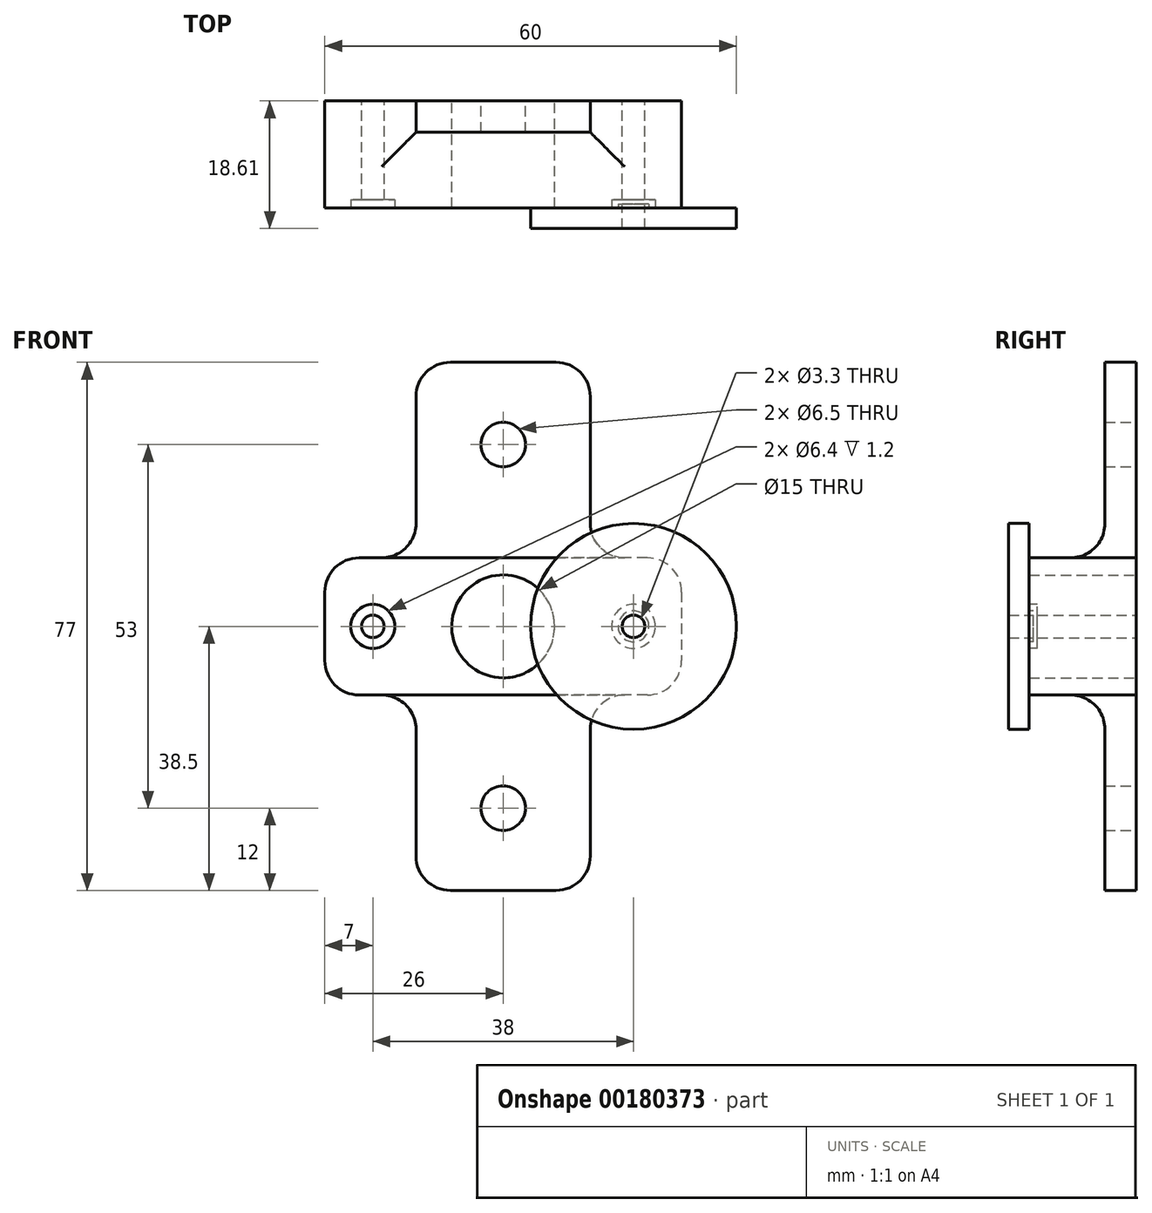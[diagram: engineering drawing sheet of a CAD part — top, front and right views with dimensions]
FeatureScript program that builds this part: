
annotation { "Feature Type Name" : "Feature", "Feature Type Description" : "" }
export const myFeature = defineFeature(function(context is Context, id is Id, definition is map)
    precondition{}
    {
        {
            var Q0;
            Q0=qCreatedBy(makeId("Front.planeOp"),FACE);
            var sketch = newSketch(context, id + "F0", { "sketchPlane" : qUnion([Q0])});
            skLineSegment(sketch, "E0.bottom", {"start": v(12.7, 38.5) * mm, "end": v(-12.7, 38.5) * mm});
            skLineSegment(sketch, "E0.top", {"start": v(12.7, -38.5) * mm, "end": v(-12.7, -38.5) * mm});
            skLineSegment(sketch, "E0.left", {"start": v(12.7, 38.5) * mm, "end": v(12.7, -38.5) * mm});
            skLineSegment(sketch, "E0.right", {"start": v(-12.7, 38.5) * mm, "end": v(-12.7, -38.5) * mm});
            skPoint(sketch, "E0.middle", {"position": v(0, 0) * mm});
            skLineSegment(sketch, "E1.bottom", {"start": v(26, 10) * mm, "end": v(-26, 10) * mm});
            skLineSegment(sketch, "E1.top", {"start": v(26, -10) * mm, "end": v(-26, -10) * mm});
            skLineSegment(sketch, "E1.left", {"start": v(26, 10) * mm, "end": v(26, -10) * mm});
            skLineSegment(sketch, "E1.right", {"start": v(-26, 10) * mm, "end": v(-26, -10) * mm});
            skCircle(sketch, "E2", {"center": v(0, 0) * mm, "radius": 7.5 * mm});
            skCircle(sketch, "E3", {"center": v(0, 26.5) * mm, "radius": 3.25 * mm});
            skLineSegment(sketch, "E4", {"start": v(0, 0) * mm, "end": v(26, 0) * mm, "construction": true});
            skCircle(sketch, "E5.MirrorC", {"center": v(0, -26.5) * mm, "radius": 3.25 * mm});
            skCircle(sketch, "E6", {"center": v(-19, 0) * mm, "radius": 1.65 * mm});
            skLineSegment(sketch, "E7", {"start": v(0, 0) * mm, "end": v(0, 26.5) * mm, "construction": true});
            skCircle(sketch, "E8.MirrorC", {"center": v(19, 0) * mm, "radius": 1.65 * mm});
            skSolve(sketch);
        }
        {
            var Q0;
            {var subQ5=sQuery(id+"F0.wireOp",EDGE,"E0.bottom");Q0=makeQuery(id+"F0.imprint","IMPRINT",FACE,{"disambiguationData":[TD([[makeQuery(id+"F0.imprint","IMPRINT",EDGE,{"derivedFrom":subQ5}),1.0]])]});}
            var Q1;
            {var subQ5=sQuery(id+"F0.wireOp",EDGE,"E0.top");Q1=makeQuery(id+"F0.imprint","IMPRINT",FACE,{"disambiguationData":[TD([[makeQuery(id+"F0.imprint","IMPRINT",EDGE,{"derivedFrom":subQ5}),-1.0]])]});}
            var Q2;
            Q2=makeQuery(id+"F0.imprint","IMPRINT",FACE,{"disambiguationData":[TD([[makeQuery(id+"F0.imprint","IMPRINT",EDGE,{"derivedFrom":sQuery(id+"F0.wireOp",EDGE,"E2")}),-1.0]])]});
            extrude(context, id + "F1", {"entities" : qUnion([Q0, Q1, Q2]), "depth" : 4.57 * mm, "offsetDistance" : 25 * mm});
        }
        {
            var Q0;
            {var subQ0=sQuery(id+"F0.wireOp",EDGE,"E1.left");Q0=makeQuery(id+"F0.imprint","IMPRINT",FACE,{"disambiguationData":[TD([[makeQuery(id+"F0.imprint","IMPRINT",EDGE,{"derivedFrom":subQ0}),-1.0]])]});}
            var Q1;
            {var subQ0=sQuery(id+"F0.wireOp",EDGE,"E1.right");Q1=makeQuery(id+"F0.imprint","IMPRINT",FACE,{"disambiguationData":[TD([[makeQuery(id+"F0.imprint","IMPRINT",EDGE,{"derivedFrom":subQ0}),1.0]])]});}
            var Q2;
            Q2=makeQuery(id+"F0.imprint","IMPRINT",FACE,{"disambiguationData":[TD([[makeQuery(id+"F0.imprint","IMPRINT",EDGE,{"derivedFrom":sQuery(id+"F0.wireOp",EDGE,"E2")}),-1.0]])]});
            extrude(context, id + "F2", {"entities" : qUnion([Q0, Q1, Q2]), "operationType" : NewBodyOperationType.ADD, "depth" : 15.6 * mm, "offsetDistance" : 25 * mm});
        }
        {
            var Q0;
            Q0=makeQuery(id+"F2.opExtrude","CAP_FACE",FACE,{"disambiguationData":[OSD([sQuery(id+"F0.wireOp",EDGE,"E1.bottom"),sQuery(id+"F0.wireOp",EDGE,"E1.top"),sQuery(id+"F0.wireOp",EDGE,"E1.left"),sQuery(id+"F0.wireOp",EDGE,"E1.right"),sQuery(id+"F0.wireOp",EDGE,"E2"),sQuery(id+"F0.wireOp",EDGE,"E6"),sQuery(id+"F0.wireOp",EDGE,"E8.MirrorC")])],"isStart":false});
            var sketch = newSketch(context, id + "F3", { "sketchPlane" : qUnion([Q0])});
            skCircle(sketch, "E9", {"center": v(19, 0) * mm, "radius": 3.2 * mm});
            skCircle(sketch, "E10", {"center": v(-19, 0) * mm, "radius": 3.2 * mm});
            skSolve(sketch);
        }
        {
            var Q0;
            Q0=makeQuery(id+"F3.imprint","IMPRINT",FACE,{"disambiguationData":[TD([[makeQuery(id+"F3.imprint","IMPRINT",EDGE,{"derivedFrom":sQuery(id+"F3.wireOp",EDGE,"E10")}),1.0]])]});
            var Q1;
            Q1=makeQuery(id+"F3.imprint","IMPRINT",FACE,{"disambiguationData":[TD([[makeQuery(id+"F3.imprint","IMPRINT",EDGE,{"derivedFrom":sQuery(id+"F3.wireOp",EDGE,"E9")}),1.0]])]});
            extrude(context, id + "F4", {"entities" : qUnion([Q0, Q1]), "operationType" : NewBodyOperationType.REMOVE, "oppositeDirection" : true, "depth" : 1.2 * mm, "offsetDistance" : 25 * mm});
        }
        {
            var Q0;
            Q0=makeQuery(id+"F2.boolean.opBoolean","INTERSECT",EDGE,{"derivedFrom":[makeQuery(id+"F1.opExtrude","CAP_FACE",FACE,{"disambiguationData":[OSD([sQuery(id+"F0.wireOp",EDGE,"E0.bottom"),sQuery(id+"F0.wireOp",EDGE,"E0.top"),sQuery(id+"F0.wireOp",EDGE,"E0.left"),sQuery(id+"F0.wireOp",EDGE,"E0.right"),sQuery(id+"F0.wireOp",EDGE,"E2"),sQuery(id+"F0.wireOp",EDGE,"E3"),sQuery(id+"F0.wireOp",EDGE,"E5.MirrorC")])],"isStart":false}),makeQuery(id+"F2.opExtrude","SWEPT_FACE",FACE,{"disambiguationData":[OSD([sQuery(id+"F0.wireOp",EDGE,"E1.bottom")])]})]});
            var Q1;
            Q1=makeQuery(id+"F2.boolean.opBoolean","INTERSECT",EDGE,{"derivedFrom":[makeQuery(id+"F1.opExtrude","CAP_FACE",FACE,{"disambiguationData":[OSD([sQuery(id+"F0.wireOp",EDGE,"E0.bottom"),sQuery(id+"F0.wireOp",EDGE,"E0.top"),sQuery(id+"F0.wireOp",EDGE,"E0.left"),sQuery(id+"F0.wireOp",EDGE,"E0.right"),sQuery(id+"F0.wireOp",EDGE,"E2"),sQuery(id+"F0.wireOp",EDGE,"E3"),sQuery(id+"F0.wireOp",EDGE,"E5.MirrorC")])],"isStart":false}),makeQuery(id+"F2.opExtrude","SWEPT_FACE",FACE,{"disambiguationData":[OSD([sQuery(id+"F0.wireOp",EDGE,"E1.top")])]})]});
            var Q2;
            Q2=makeQuery(id+"F2.opExtrude","SWEPT_EDGE",EDGE,{"disambiguationData":[OSD([sQuery(id+"F0.wireOp",EDGE,"E1.top"),sQuery(id+"F0.wireOp",EDGE,"E1.left")])]});
            var Q3;
            Q3=makeQuery(id+"F2.opExtrude","SWEPT_EDGE",EDGE,{"disambiguationData":[OSD([sQuery(id+"F0.wireOp",EDGE,"E1.top"),sQuery(id+"F0.wireOp",EDGE,"E1.right")])]});
            var Q4;
            Q4=makeQuery(id+"F2.opExtrude","SWEPT_EDGE",EDGE,{"disambiguationData":[OSD([sQuery(id+"F0.wireOp",EDGE,"E1.bottom"),sQuery(id+"F0.wireOp",EDGE,"E1.right")])]});
            var Q5;
            Q5=makeQuery(id+"F2.opExtrude","SWEPT_EDGE",EDGE,{"disambiguationData":[OSD([sQuery(id+"F0.wireOp",EDGE,"E1.bottom"),sQuery(id+"F0.wireOp",EDGE,"E1.left")])]});
            var Q6;
            Q6=makeQuery(id+"F2.boolean.opBoolean","INTERSECT",EDGE,{"derivedFrom":[makeQuery(id+"F1.opExtrude","SWEPT_FACE",FACE,{"disambiguationData":[OSD([sQuery(id+"F0.wireOp",EDGE,"E0.right")])]}),makeQuery(id+"F2.opExtrude","SWEPT_FACE",FACE,{"disambiguationData":[OSD([sQuery(id+"F0.wireOp",EDGE,"E1.bottom")])]})]});
            var Q7;
            Q7=makeQuery(id+"F2.boolean.opBoolean","INTERSECT",EDGE,{"derivedFrom":[makeQuery(id+"F1.opExtrude","SWEPT_FACE",FACE,{"disambiguationData":[OSD([sQuery(id+"F0.wireOp",EDGE,"E0.left")])]}),makeQuery(id+"F2.opExtrude","SWEPT_FACE",FACE,{"disambiguationData":[OSD([sQuery(id+"F0.wireOp",EDGE,"E1.bottom")])]})]});
            var Q8;
            Q8=makeQuery(id+"F2.boolean.opBoolean","INTERSECT",EDGE,{"derivedFrom":[makeQuery(id+"F1.opExtrude","SWEPT_FACE",FACE,{"disambiguationData":[OSD([sQuery(id+"F0.wireOp",EDGE,"E0.left")])]}),makeQuery(id+"F2.opExtrude","SWEPT_FACE",FACE,{"disambiguationData":[OSD([sQuery(id+"F0.wireOp",EDGE,"E1.top")])]})]});
            var Q9;
            Q9=makeQuery(id+"F2.boolean.opBoolean","INTERSECT",EDGE,{"derivedFrom":[makeQuery(id+"F1.opExtrude","SWEPT_FACE",FACE,{"disambiguationData":[OSD([sQuery(id+"F0.wireOp",EDGE,"E0.right")])]}),makeQuery(id+"F2.opExtrude","SWEPT_FACE",FACE,{"disambiguationData":[OSD([sQuery(id+"F0.wireOp",EDGE,"E1.top")])]})]});
            var Q10;
            Q10=makeQuery(id+"F1.opExtrude","SWEPT_EDGE",EDGE,{"disambiguationData":[OSD([sQuery(id+"F0.wireOp",EDGE,"E0.bottom"),sQuery(id+"F0.wireOp",EDGE,"E0.left")])]});
            var Q11;
            Q11=makeQuery(id+"F1.opExtrude","SWEPT_EDGE",EDGE,{"disambiguationData":[OSD([sQuery(id+"F0.wireOp",EDGE,"E0.bottom"),sQuery(id+"F0.wireOp",EDGE,"E0.right")])]});
            var Q12;
            Q12=makeQuery(id+"F1.opExtrude","SWEPT_EDGE",EDGE,{"disambiguationData":[OSD([sQuery(id+"F0.wireOp",EDGE,"E0.top"),sQuery(id+"F0.wireOp",EDGE,"E0.left")])]});
            var Q13;
            Q13=makeQuery(id+"F1.opExtrude","SWEPT_EDGE",EDGE,{"disambiguationData":[OSD([sQuery(id+"F0.wireOp",EDGE,"E0.top"),sQuery(id+"F0.wireOp",EDGE,"E0.right")])]});
            fillet(context, id + "F5", {"entities" : qUnion([Q0, Q1, Q2, Q3, Q4, Q5, Q6, Q7, Q8, Q9, Q10, Q11, Q12, Q13]), "radius" : 5 * mm, "tangentPropagation" : true, "allowEdgeOverflow" : false});
        }
        {
            var Q0;
            Q0=makeQuery(id+"F2.opExtrude","CAP_FACE",FACE,{"disambiguationData":[OSD([sQuery(id+"F0.wireOp",EDGE,"E1.bottom"),sQuery(id+"F0.wireOp",EDGE,"E1.top"),sQuery(id+"F0.wireOp",EDGE,"E1.left"),sQuery(id+"F0.wireOp",EDGE,"E1.right"),sQuery(id+"F0.wireOp",EDGE,"E2"),sQuery(id+"F0.wireOp",EDGE,"E6"),sQuery(id+"F0.wireOp",EDGE,"E8.MirrorC")])],"isStart":false});
            cPlane(context, id + "F6", {"entities" : qUnion([Q0]), "cplaneType" : CPlaneType.OFFSET, "offset" : 7 / 812.8 * mm, "width" : 150 * mm, "height" : 150 * mm});
        }
        {
            var Q0;
            Q0=qCreatedBy(id+"F6.planeOp",FACE);
            var sketch = newSketch(context, id + "F7", { "sketchPlane" : qUnion([Q0])});
            skCircle(sketch, "E11.0", {"center": v(19, 0) * mm, "radius": 1.65 * mm});
            skCircle(sketch, "E12", {"center": v(19, 0) * mm, "radius": 15 * mm});
            skCircle(sketch, "E13", {"center": v(19, 0) * mm, "radius": 2.25 * mm});
            skSolve(sketch);
        }
        {
            var Q0;
            Q0=makeQuery(id+"F7.imprint","IMPRINT",FACE,{"disambiguationData":[TD([[makeQuery(id+"F7.imprint","IMPRINT",EDGE,{"derivedFrom":sQuery(id+"F7.wireOp",EDGE,"E12")}),1.0]])]});
            var Q1;
            Q1=makeQuery(id+"F7.imprint","IMPRINT",FACE,{"disambiguationData":[TD([[makeQuery(id+"F7.imprint","IMPRINT",EDGE,{"derivedFrom":sQuery(id+"F7.wireOp",EDGE,"E11.0")}),-1.0]])]});
            extrude(context, id + "F8", {"entities" : qUnion([Q0, Q1]), "depth" : 3 * mm, "offsetDistance" : 25 * mm});
        }
        {
            var Q0;
            Q0=makeQuery(id+"F7.imprint","IMPRINT",FACE,{"disambiguationData":[TD([[makeQuery(id+"F7.imprint","IMPRINT",EDGE,{"derivedFrom":sQuery(id+"F7.wireOp",EDGE,"E11.0")}),-1.0]])]});
            extrude(context, id + "F9", {"entities" : qUnion([Q0]), "operationType" : NewBodyOperationType.ADD, "oppositeDirection" : true, "depth" : 0.6 * mm, "offsetDistance" : 25 * mm});
        }
    });
